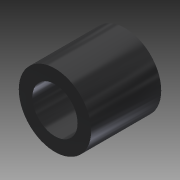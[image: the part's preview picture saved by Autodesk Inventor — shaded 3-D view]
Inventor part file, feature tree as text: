
AUTODESK INVENTOR PART (.ipt)
format: ipt  version: 2014 (Build 180170000, 170)  size: 81,408 bytes
history: native  units: in
note: dims shown in document units (in); Inventor stores cm internally (conversion verified against a paired STEP export)
features: extrude x1, sketch x1
ambient origin geometry x8: Origin, YZ Plane, XZ Plane, XY Plane, X Axis, Y Axis, Z Axis, Center Point
bodies: Solid1 (feature_tree)
feature tree (2):
  extrude  "Extrusion1"  Depth=1.94in
  sketch  "Sketch1"  dims[d0=2.0in d1=1.25in d2=1.94in d3=0.0in]
